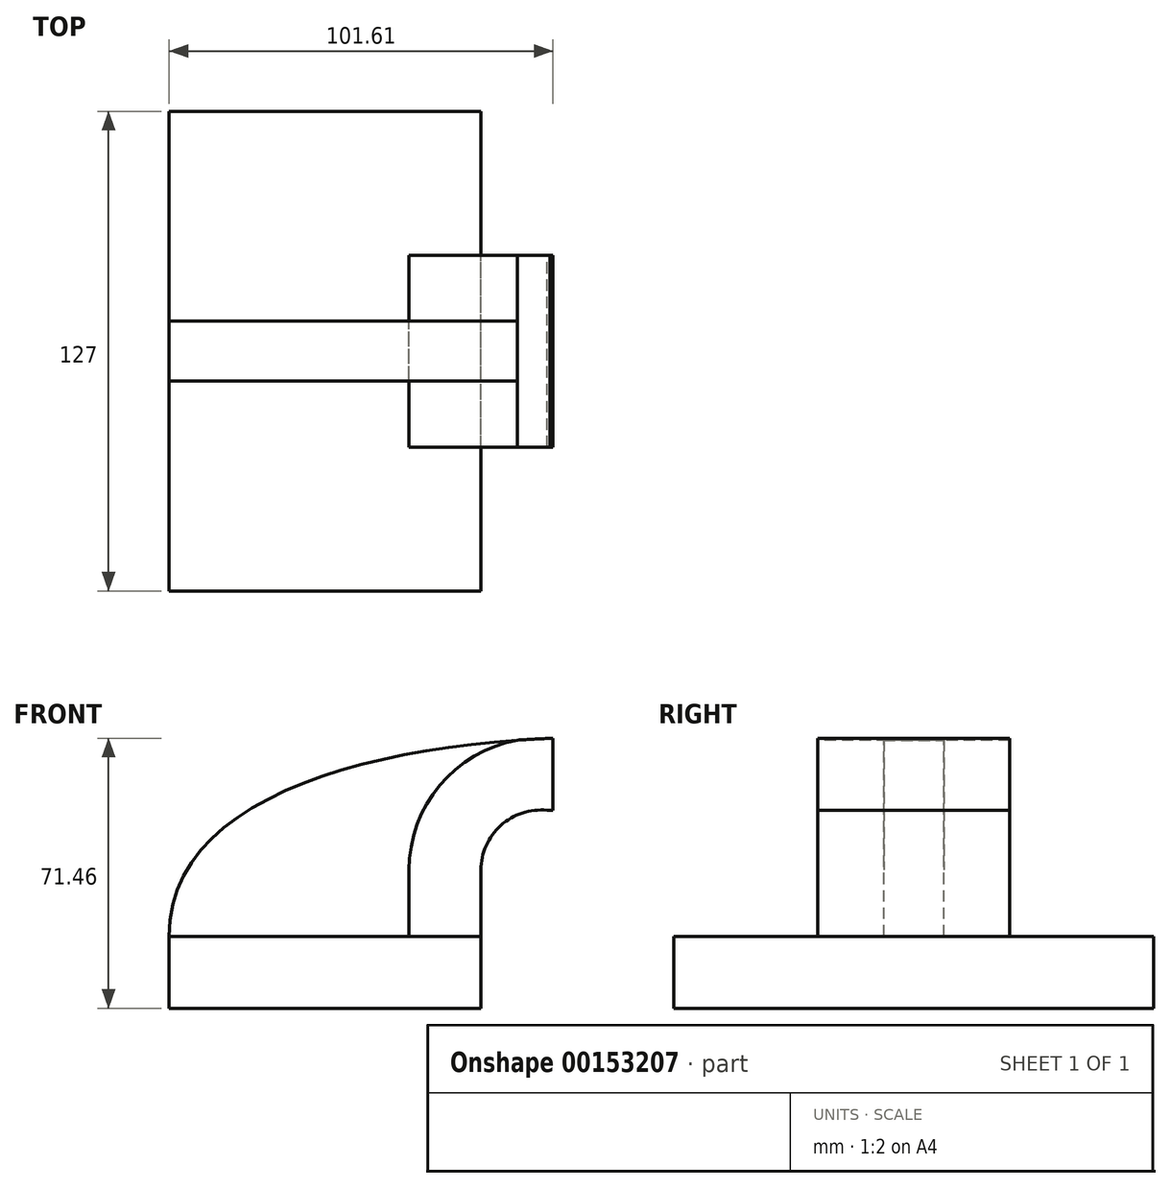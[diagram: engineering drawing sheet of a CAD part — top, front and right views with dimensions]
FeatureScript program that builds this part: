
annotation { "Feature Type Name" : "Feature", "Feature Type Description" : "" }
export const myFeature = defineFeature(function(context is Context, id is Id, definition is map)
    precondition{}
    {
        {
            var Q0;
            Q0=qCreatedBy(makeId("Front.planeOp"),FACE);
            var sketch = newSketch(context, id + "F0", { "sketchPlane" : qUnion([Q0])});
            skLineSegment(sketch, "E0.bottom", {"start": v(-41.28, 9.52) * mm, "end": v(41.27, 9.53) * mm});
            skLineSegment(sketch, "E0.top", {"start": v(-41.28, -9.53) * mm, "end": v(41.28, -9.53) * mm});
            skLineSegment(sketch, "E0.left", {"start": v(-41.28, 9.52) * mm, "end": v(-41.27, -9.53) * mm});
            skLineSegment(sketch, "E0.right", {"start": v(41.28, 9.53) * mm, "end": v(41.28, -9.52) * mm});
            skPoint(sketch, "E0.middle", {"position": v(0, 0) * mm});
            skLineSegment(sketch, "E1.bottom", {"start": v(60.33, 66.67) * mm, "end": v(111.12, 66.67) * mm});
            skLineSegment(sketch, "E1.top", {"start": v(60.33, 38.1) * mm, "end": v(111.13, 38.1) * mm});
            skLineSegment(sketch, "E1.left", {"start": v(60.33, 66.67) * mm, "end": v(60.33, 38.1) * mm});
            skLineSegment(sketch, "E1.right", {"start": v(111.13, 66.67) * mm, "end": v(111.13, 38.1) * mm});
            skPoint(sketch, "E1.middle", {"position": v(85.73, 52.39) * mm});
            skLineSegment(sketch, "E2", {"start": v(41.27, 9.53) * mm, "end": v(41.27, 27.08) * mm});
            skArc(sketch, "E3", {"start": v(41.27, 27.08) * mm, "mid": v(46.5, 38.85) * mm, "end": v(58.74, 42.88) * mm});
            skLineSegment(sketch, "E4", {"start": v(58.74, 42.88) * mm, "end": v(100.15, 42.88) * mm});
            skLineSegment(sketch, "E5.0", {"start": v(59.5, 61.93) * mm, "end": v(100.15, 61.93) * mm});
            skArc(sketch, "E5.1", {"start": v(22.22, 27.08) * mm, "mid": v(33.3, 52.6) * mm, "end": v(59.5, 61.93) * mm});
            skLineSegment(sketch, "E5.2", {"start": v(22.23, 9.53) * mm, "end": v(22.23, 27.08) * mm});
            skLineSegment(sketch, "E6", {"start": v(100.15, 61.93) * mm, "end": v(100.15, 42.88) * mm});
            skFitSpline(sketch, "E7", {"points": [v(-41.28, 9.52) * mm, v(59.5, 61.93) * mm], "startDerivative": vector(-0.72, 108) * mm, "endDerivative": vector(149.26, 6.26) * mm});
            skLineSegment(sketch, "E8", {"start": v(85.73, 52.39) * mm, "end": v(85.73, 38.1) * mm});
            skLineSegment(sketch, "E9", {"start": v(85.72, 52.39) * mm, "end": v(85.72, 66.67) * mm});
            skLineSegment(sketch, "E10", {"start": v(85.73, 38.1) * mm, "end": v(85.72, 66.67) * mm});
            skSolve(sketch);
        }
        {
            var Q0;
            Q0=makeQuery(id+"F0.imprint","IMPRINT",FACE,{"disambiguationData":[TD([[makeQuery(id+"F0.imprint","IMPRINT",EDGE,{"derivedFrom":sQuery(id+"F0.wireOp",EDGE,"E0.top")}),1.0]])]});
            extrude(context, id + "F1", {"entities" : qUnion([Q0]), "endBound" : BoundingType.SYMMETRIC, "depth" : 127 * mm});
        }
        {
            var Q0;
            {var subQ1=sQuery(id+"F0.wireOp",EDGE,"E2");Q0=makeQuery(id+"F0.imprint","IMPRINT",FACE,{"disambiguationData":[TD([[makeQuery(id+"F0.imprint","IMPRINT",EDGE,{"derivedFrom":subQ1}),1.0]])]});}
            var Q1;
            {var subQ0=sQuery(id+"F0.wireOp",EDGE,"E10");var subQ1=makeQuery(id+"F0.imprint","IMPRINT",VERTEX,{"derivedFrom":subQ0});Q1=makeQuery(id+"F0.imprint","IMPRINT",FACE,{"disambiguationData":[TD([[makeQuery(id+"F0.imprint","IMPRINT",EDGE,{"disambiguationData":[TD([[subQ1,1.0]])],"derivedFrom":subQ0}),1.0]])]});}
            extrude(context, id + "F2", {"entities" : qUnion([Q0, Q1]), "endBound" : BoundingType.SYMMETRIC, "depth" : 50.8 * mm});
        }
        {
            var Q0;
            {var subQ3=sQuery(id+"F0.wireOp",EDGE,"E5.2");Q0=makeQuery(id+"F0.imprint","IMPRINT",FACE,{"disambiguationData":[TD([[makeQuery(id+"F0.imprint","IMPRINT",EDGE,{"derivedFrom":subQ3}),1.0]])]});}
            extrude(context, id + "F3", {"entities" : qUnion([Q0]), "endBound" : BoundingType.SYMMETRIC, "depth" : 15.88 * mm});
        }
    });
